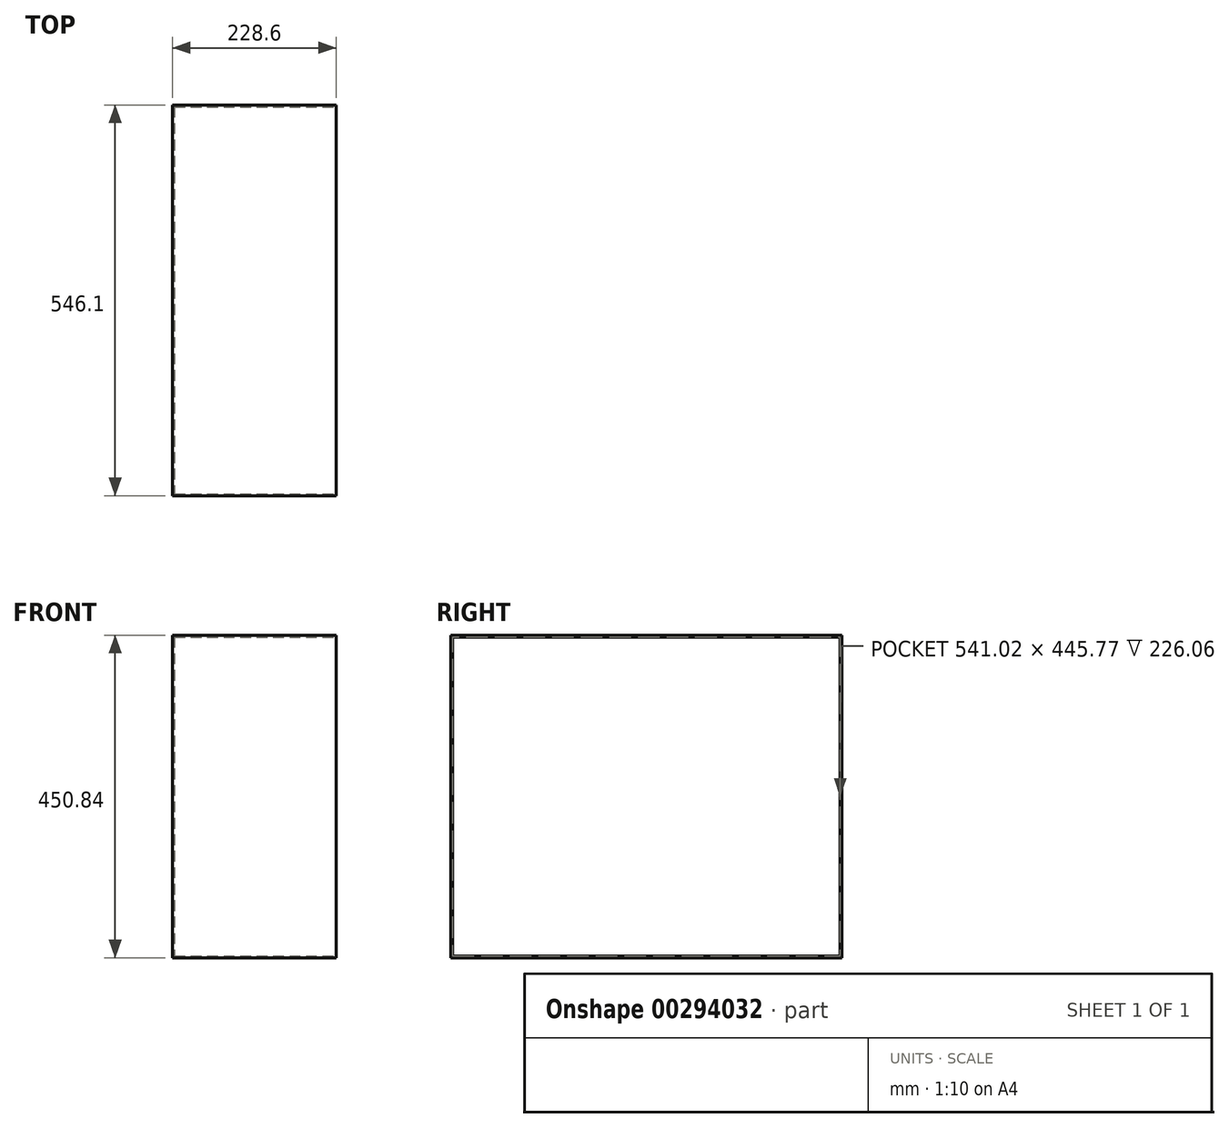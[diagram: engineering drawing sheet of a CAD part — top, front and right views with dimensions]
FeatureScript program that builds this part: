
annotation { "Feature Type Name" : "Feature", "Feature Type Description" : "" }
export const myFeature = defineFeature(function(context is Context, id is Id, definition is map)
    precondition{}
    {
        {
            var Q0;
            Q0=qCreatedBy(makeId("Front.planeOp"),FACE);
            var sketch = newSketch(context, id + "F0", { "sketchPlane" : qUnion([Q0])});
            skLineSegment(sketch, "E0.bottom", {"start": v(-114.3, 225.43) * mm, "end": v(114.3, 225.43) * mm});
            skLineSegment(sketch, "E0.top", {"start": v(-114.3, -225.43) * mm, "end": v(114.3, -225.43) * mm});
            skLineSegment(sketch, "E0.left", {"start": v(-114.3, 225.43) * mm, "end": v(-114.3, -225.43) * mm});
            skLineSegment(sketch, "E0.right", {"start": v(114.3, 225.42) * mm, "end": v(114.3, -225.43) * mm});
            skPoint(sketch, "E0.middle", {"position": v(0, 0) * mm});
            skSolve(sketch);
        }
        {
            var Q0;
            Q0 = qSketchRegion(id + "F0", true);
            extrude(context, id + "F1", {"entities" : qUnion([Q0]), "oppositeDirection" : true, "depth" : 546.1 * mm});
        }
        {
            var Q0;
            Q0=makeQuery(id+"F1.opExtrude","SWEPT_FACE",FACE,{"disambiguationData":[OSD([sQuery(id+"F0.wireOp",EDGE,"E0.right")])]});
            shell(context, id + "F2", {"entities" : qUnion([Q0]), "thickness" : 2.54 * mm});
        }
    });
